# Revit family: 1058xxx Enna Square Switched LED (UL) New
name_source: partatom
category: Lighting Fixtures
units: mm (PartAtom-declared; Revit-internal decimal feet)

## family parameters
Always vertical = Yes
Cut with Voids When Loaded = No
Host = Wall
Light Source = Yes
OmniClass Number = 23.80.70.00
OmniClass Title = Lighting
Part Type = Normal
Room Calculation Point = No
Round Connector Dimension = Use Diameter
Shared = No

## types (5) — shared parameters
ADA compliant = Yes - if installed in compliance with
Yes - if installed in compliance with  ADA 307.2, 308, 309.3, 309.4
Apparent Load = 10 VA
Color Filter = 16777215
Dimmable = No
Dimming Lamp Color Temperature Shift = <None>
Driver Included = Yes
Driver Required = No
Efficacy (lm/w) = 25
Electrical Class = 1
Emit from Line Length = 610 mm
Lamp = 2 Watt LED
Length of Cable Supplied = 150mm
Light Source Fixed = yes
Location / IP Rating = DRY
Main Material = Metal - Aluminium / Zinc / Steel
Manufacturer = Astro Lighting Ltd
Manufacturer URL - Europe and Rest of World = www.astrolighting.com
Manufacturer URL - North America = us.astrolighting.com
Photometric Web File = TRN-18496  Enna Recess Switched.ies
Power (Watts) = 4.47
Product CCT = 2700K
Product CRI = 90
Product Dimensions (INCH) = 4.33 x 4.33 x 5.12
Product Location = Bedroom / Wall
Product Name = Enna Square Switched LED
Product URL = https://us.astrolighting.com
Product Weight (LB) = 1.56
Tilt Angle = 60.00°
URL = www.astrolighting.com
zero-valued in all types: Default Elevation

## per-type parameters (varying)
| type | Main Finish | Product SKU |
| Enna Square Switched LED - Matt Black | Matt Black | 1058049 |
| Enna Square Switched LED - Matt Gold | Matt Gold | 1058044 |
| Enna Square Switched LED - Matt Nickel | Matt Nickel | 1058046 |
| Enna Square Switched LED - Textured White | Textured White | 1058048 |
| Enna Square Switched LED - Polished Chrome | Polished Chrome | 1058047 |

## geometry (parser evidence)
native form markers: Sweep x2
no freeform markers — native parametric forms only
